# Revit family: 210_101d5c66d62c43bfbcc20518987600
name_source: partatom
category: Mechanical Equipment
revit_build: Autodesk Revit 2017 (Build: 20160225_1515(x64)
units: mm (PartAtom-declared; Revit-internal decimal feet)

## family parameters
Always vertical = Yes
Cut with Voids When Loaded = No
Part Type = Breaks Into
Room Calculation Point = No
Round Connector Dimension = Use Diameter
Shared = No
Work Plane-Based = No

## types (1)
- Nordic S2 R_L (800113)
    Clearance Zone Front Depth = 500 mm  [stored 1.64042 ft]
    D = 125 mm
    DC = 125 mm
    DH = 25 mm  [stored 0.082021 ft]
    DL = 64 mm  [stored 0.209974 ft]
    DW = 30 mm  [stored 0.0984252 ft]
    Description = Nordic S2 R_L (800113)
    H = 777 mm  [stored 2.54921 ft]
    HB = 700 mm  [stored 2.29659 ft]
    HD = 125 mm  [stored 0.410105 ft]
    L2 = 300 mm  [stored 0.984252 ft]
    LD = 35 mm  [stored 0.114829 ft]
    MC Product Code = Nordic S2 R_L (800113)
    Manufacturer = Flexit
    QmdConnectorList = 221;D;231;D;241;D;249;DC;251;D
    R = 63 mm
    R1 = 78 mm
    RC = 63 mm
    W = 500 mm  [stored 1.64042 ft]
    W0 = 518 mm  [stored 1.69948 ft]
    W2 = 264 mm  [stored 0.866142 ft]
    XEXH = 110 mm  [stored 0.360892 ft]
    XEXT = 490 mm  [stored 1.60761 ft]
    XK = 300 mm  [stored 0.984252 ft]
    XL = 250 mm  [stored 0.82021 ft]
    XOUT = 110 mm  [stored 0.360892 ft]
    XSUP = 490 mm  [stored 1.60761 ft]
    XT = 50 mm  [stored 0.164042 ft]
    YEXH = 120 mm  [stored 0.393701 ft]
    YEXT = 120 mm  [stored 0.393701 ft]
    YK = 215 mm  [stored 0.705381 ft]
    YL = 508 mm  [stored 1.66667 ft]
    YOUT = 370 mm  [stored 1.21391 ft]
    YSUP = 370 mm  [stored 1.21391 ft]
    magiPartTypeId = 210
    magiProductFamilyId = 101d5c66d62c43bfbcc20518987600
    magiProductId = 101d5c66d62c43bfbcc20518987600

note: [stored X ft] marks values corroborated as IEEE doubles in the binary element streams (Revit-internal decimal feet)

## geometry (parser evidence)
native form markers: Sweep x1
no freeform markers — native parametric forms only
